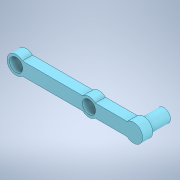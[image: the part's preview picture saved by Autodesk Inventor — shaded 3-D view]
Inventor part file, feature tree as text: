
AUTODESK INVENTOR PART (.ipt)
format: ipt  version: 2022 (Build 260153000, 153)  size: 140,288 bytes
history: native  units: in
note: dims shown in document units (in); Inventor stores cm internally (conversion verified against a paired STEP export)
features: extrude x2, sketch x1
ambient origin geometry x8: Origin, YZ Plane, XZ Plane, XY Plane, X Axis, Y Axis, Z Axis, Center Point
bodies: Solid1 (feature_tree)
feature tree (3):
  sketch  "Sketch2"  dims[d0=0.1969in d1=0.0in d2=0.3937in d3=0.0in d4=0.8661in d5=1.4173in d6=0.2559in d7=0.3543in d8=0.2559in]
  extrude  "Extrusion1"  Depth=0.3937in TaperAngle=0.0deg
  extrude  "Extrusion2"  Depth=0.2559in
